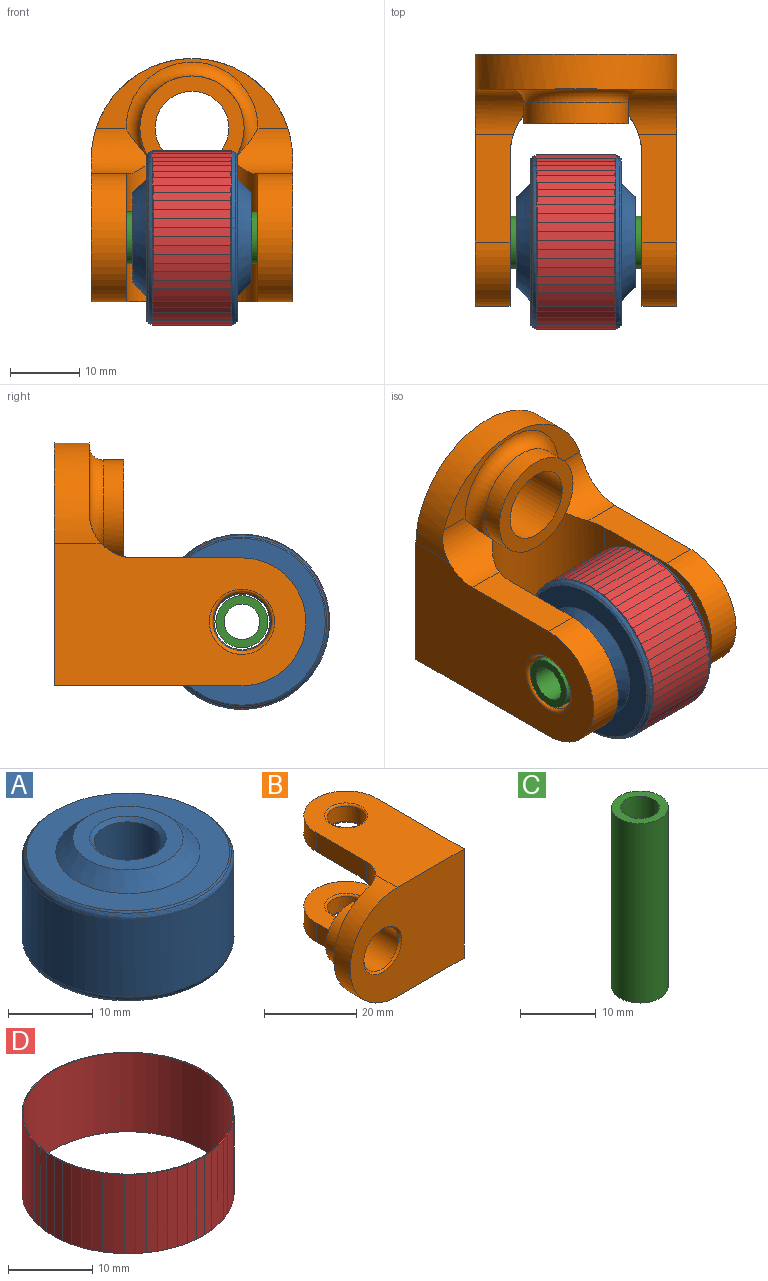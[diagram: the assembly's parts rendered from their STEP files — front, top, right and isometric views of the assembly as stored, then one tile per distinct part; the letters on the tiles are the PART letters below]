
ASSEMBLY  parts=4 mates=3
PART A: 14 faces, bbox 27.1x27.1x17 mm
  f0: cylinder r=4mm len=16mm, axis (0,0,-1), area 402.1mm2, adj f10,f11
  f1: cylinder r=12.5mm len=25mm, axis (0,0,-1), area 877.4mm2, adj f6,f7
  f2: plane 24x24mm, normal (0,0,1), area 225.4mm2, adj f5,f13
  f3: plane 24x24mm, normal (0,0,-1), area 225.4mm2, adj f4,f12
  f4: cone r=12.5mm half-angle=45deg, axis (0,0,1), area 22.3mm2, adj f3,f6
  f5: cone r=12mm half-angle=45deg, axis (0,0,-1), area 22.3mm2, adj f2,f7
  f6: torus R=11.5mm, axis (0,0,-1), area 61.2mm2, adj f1,f4
  f7: torus R=11.5mm, axis (0,0,1), area 61.2mm2, adj f1,f5
  f8: plane 13x13mm, normal (0,0,1), area 69.1mm2, adj f10,f13
  f9: plane 13x13mm, normal (0,0,-1), area 69.1mm2, adj f11,f12
  f10: cone r=4mm half-angle=45deg, axis (0,0,1), area 18.9mm2, adj f0,f8
  f11: cone r=4.5mm half-angle=45deg, axis (0,0,-1), area 18.9mm2, adj f0,f9
  f12: cone r=8.5mm half-angle=45deg, axis (0,0,1), area 133.3mm2, adj f3,f9
  f13: cone r=6.5mm half-angle=45deg, axis (0,0,-1), area 133.3mm2, adj f2,f8
PART B: 26 faces, bbox 36.8x36.2x29 mm
  f0: plane 29x27mm, normal (1,0,0), area 403.7mm2, adj f1,f4,f5,f9,f12,f13,f17,f21
  f1: cylinder r=9.2mm len=18.4mm, axis (0,0,-1), area 144.5mm2, adj f0,f3,f4,f5
  f2: cylinder r=4.2mm len=8.4mm, axis (0,0,-1), area 105.6mm2, adj f6,f7
  f3: plane 15.5x5.49mm, normal (-1,0,0), area 78mm2, adj f1,f4,f5,f21,f25
  f4: plane 36.2x20.5mm, normal (0,0,1), area 577.6mm2, adj f0,f1,f3,f7,f17,f22,f25
  f5: plane 21.7x18.4mm, normal (0,0,-1), area 293.6mm2, adj f0,f1,f3,f6,f21
  f6: torus R=4.7mm, axis (0,0,1), area 21.6mm2, adj f2,f5
  f7: torus R=4.7mm, axis (0,0,1), area 21.6mm2, adj f2,f4
  f8: plane 27.63x10.1mm, normal (0,1,0), area 61mm2, adj f20,f22,f24,f25
  f9: cylinder r=9.2mm len=18.4mm, axis (0,0,-1), area 144.5mm2, adj f0,f11,f12,f13
  f10: cylinder r=4.2mm len=8.4mm, axis (0,0,-1), area 105.6mm2, adj f14,f15
  f11: plane 15.5x5.49mm, normal (-1,0,0), area 78mm2, adj f9,f12,f13,f21,f24
  f12: plane 21.7x18.4mm, normal (0,0,1), area 293.6mm2, adj f0,f9,f11,f15,f21
  f13: plane 36.2x20.5mm, normal (0,0,-1), area 577.6mm2, adj f0,f9,f11,f14,f17,f22,f24
  f14: torus R=4.7mm, axis (0,0,1), area 21.6mm2, adj f10,f13
  f15: torus R=4.7mm, axis (0,0,1), area 21.6mm2, adj f10,f12
  f16: cylinder r=5.3mm len=10.6mm, axis (0,1,0), area 316.4mm2, adj f19,f23
  f17: plane 35x29mm, normal (0,-1,0), area 819.1mm2, adj f0,f4,f13,f22,f23
  f18: cylinder r=7.5mm len=15mm, axis (0,-1,0), area 141.4mm2, adj f19,f20
  f19: plane 15x15mm, normal (0,1,0), area 88.5mm2, adj f16,f18
  f20: torus R=9.5mm, axis (0,-1,0), area 119.9mm2, adj f8,f18,f21,f24,f25
  f21: cylinder r=9.5mm len=20.24mm, axis (-1,0,0), area 546.1mm2, adj f0,f3,f5,f11,f12,f20,f24,f25
  f22: cylinder r=14.5mm len=29mm, axis (0,1,0), area 232.5mm2, adj f4,f8,f13,f17,f24,f25
  f23: cone r=5.3mm half-angle=45deg, axis (0,-1,0), area 24.7mm2, adj f16,f17
  f24: cylinder r=6.5mm len=8.71mm, axis (0,0,-1), area 68.7mm2, adj f8,f11,f13,f20,f21,f22
  f25: cylinder r=6.5mm len=8.71mm, axis (0,0,-1), area 68.7mm2, adj f3,f4,f8,f20,f21,f22
PART C: 4 faces, bbox 7.5x7.5x29 mm
  f0: cylinder r=2.55mm len=29mm, axis (0,0,-1), area 464.6mm2, adj f2,f3
  f1: cylinder r=3.75mm len=29mm, axis (0,0,-1), area 683.3mm2, adj f2,f3
  f2: plane 7.5x7.5mm, normal (0,0,1), area 23.8mm2, adj f0,f1
  f3: plane 7.5x7.5mm, normal (0,0,-1), area 23.8mm2, adj f0,f1
PART D: 63 faces, bbox 25.2x25.2x11.5 mm
  f0: plane 11.5x1.04mm, normal (0.62,0.79,0), area 15.2mm2, adj f1,f60,f61,f62
  f1: plane 11.5x1.12mm, normal (0.53,0.85,0), area 15.2mm2, adj f0,f2,f61,f62
  f2: plane 11.5x1.19mm, normal (0.44,0.9,0), area 15.2mm2, adj f1,f3,f61,f62
  f3: plane 11.5x1.24mm, normal (0.34,0.94,0), area 15.2mm2, adj f2,f4,f61,f62
  f4: plane 11.5x1.28mm, normal (0.24,0.97,0), area 15.2mm2, adj f3,f5,f61,f62
  f5: plane 11.5x1.31mm, normal (0.14,0.99,0), area 15.2mm2, adj f4,f6,f61,f62
  f6: plane 11.5x1.32mm, normal (0.03,1,0), area 15.2mm2, adj f5,f7,f61,f62
  f7: plane 11.5x1.32mm, normal (-0.07,1,0), area 15.2mm2, adj f6,f8,f61,f62
  f8: plane 11.5x1.3mm, normal (-0.17,0.98,0), area 15.2mm2, adj f7,f9,f61,f62
  f9: plane 11.5x1.27mm, normal (-0.28,0.96,0), area 15.2mm2, adj f8,f10,f61,f62
  f10: plane 11.5x1.22mm, normal (-0.38,0.93,0), area 15.2mm2, adj f9,f11,f61,f62
  f11: plane 11.5x1.17mm, normal (-0.47,0.88,0), area 15.2mm2, adj f10,f12,f61,f62
  f12: plane 11.5x1.09mm, normal (-0.56,0.83,0), area 15.2mm2, adj f11,f13,f61,f62
  f13: plane 11.5x1.01mm, normal (-0.64,0.77,0), area 15.2mm2, adj f12,f14,f61,f62
  f14: plane 11.5x0.95mm, normal (-0.72,0.69,0), area 15.2mm2, adj f13,f15,f61,f62
  f15: plane 11.5x1.04mm, normal (-0.79,0.62,0), area 15.2mm2, adj f14,f16,f61,f62
  f16: plane 11.5x1.12mm, normal (-0.85,0.53,0), area 15.2mm2, adj f15,f17,f61,f62
  f17: plane 11.5x1.19mm, normal (-0.9,0.44,0), area 15.2mm2, adj f16,f18,f61,f62
  f18: plane 11.5x1.24mm, normal (-0.94,0.34,0), area 15.2mm2, adj f17,f19,f61,f62
  f19: plane 11.5x1.28mm, normal (-0.97,0.24,0), area 15.2mm2, adj f18,f20,f61,f62
  f20: plane 11.5x1.31mm, normal (-0.99,0.14,0), area 15.2mm2, adj f19,f21,f61,f62
  f21: plane 11.5x1.32mm, normal (-1,0.03,0), area 15.2mm2, adj f20,f22,f61,f62
  f22: plane 11.5x1.32mm, normal (-1,-0.07,0), area 15.2mm2, adj f21,f23,f61,f62
  f23: plane 11.5x1.3mm, normal (-0.98,-0.17,0), area 15.2mm2, adj f22,f24,f61,f62
  f24: plane 11.5x1.27mm, normal (-0.96,-0.28,0), area 15.2mm2, adj f23,f25,f61,f62
  f25: plane 11.5x1.22mm, normal (-0.93,-0.38,0), area 15.2mm2, adj f24,f26,f61,f62
  f26: plane 11.5x1.17mm, normal (-0.88,-0.47,0), area 15.2mm2, adj f25,f27,f61,f62
  f27: plane 11.5x1.09mm, normal (-0.83,-0.56,0), area 15.2mm2, adj f26,f28,f61,f62
  f28: plane 11.5x1.01mm, normal (-0.77,-0.64,0), area 15.2mm2, adj f27,f29,f61,f62
  f29: plane 11.5x0.95mm, normal (-0.69,-0.72,0), area 15.2mm2, adj f28,f30,f61,f62
  f30: plane 11.5x1.04mm, normal (-0.62,-0.79,0), area 15.2mm2, adj f29,f31,f61,f62
  f31: plane 11.5x1.12mm, normal (-0.53,-0.85,0), area 15.2mm2, adj f30,f32,f61,f62
  f32: plane 11.5x1.19mm, normal (-0.44,-0.9,0), area 15.2mm2, adj f31,f33,f61,f62
  f33: plane 11.5x1.24mm, normal (-0.34,-0.94,0), area 15.2mm2, adj f32,f34,f61,f62
  f34: plane 11.5x1.28mm, normal (-0.24,-0.97,0), area 15.2mm2, adj f33,f35,f61,f62
  f35: plane 11.5x1.31mm, normal (-0.14,-0.99,0), area 15.2mm2, adj f34,f36,f61,f62
  f36: plane 11.5x1.32mm, normal (-0.03,-1,0), area 15.2mm2, adj f35,f37,f61,f62
  f37: plane 11.5x1.32mm, normal (0.07,-1,0), area 15.2mm2, adj f36,f38,f61,f62
  f38: plane 11.5x1.3mm, normal (0.17,-0.98,0), area 15.2mm2, adj f37,f39,f61,f62
  f39: plane 11.5x1.27mm, normal (0.28,-0.96,0), area 15.2mm2, adj f38,f40,f61,f62
  f40: plane 11.5x1.22mm, normal (0.38,-0.93,0), area 15.2mm2, adj f39,f41,f61,f62
  f41: plane 11.5x1.17mm, normal (0.47,-0.88,0), area 15.2mm2, adj f40,f42,f61,f62
  f42: plane 11.5x1.09mm, normal (0.56,-0.83,0), area 15.2mm2, adj f41,f43,f61,f62
  f43: plane 11.5x1.01mm, normal (0.64,-0.77,0), area 15.2mm2, adj f42,f44,f61,f62
  f44: plane 11.5x0.95mm, normal (0.72,-0.69,0), area 15.2mm2, adj f43,f45,f61,f62
  f45: plane 11.5x1.04mm, normal (0.79,-0.62,0), area 15.2mm2, adj f44,f46,f61,f62
  f46: plane 11.5x1.12mm, normal (0.85,-0.53,0), area 15.2mm2, adj f45,f47,f61,f62
  f47: plane 11.5x1.19mm, normal (0.9,-0.44,0), area 15.2mm2, adj f46,f48,f61,f62
  f48: plane 11.5x1.24mm, normal (0.94,-0.34,0), area 15.2mm2, adj f47,f49,f61,f62
  f49: plane 11.5x1.28mm, normal (0.97,-0.24,0), area 15.2mm2, adj f48,f50,f61,f62
  f50: plane 11.5x1.31mm, normal (0.99,-0.14,0), area 15.2mm2, adj f49,f51,f61,f62
  f51: plane 11.5x1.32mm, normal (1,-0.03,0), area 15.2mm2, adj f50,f52,f61,f62
  f52: plane 11.5x1.32mm, normal (1,0.07,0), area 15.2mm2, adj f51,f53,f61,f62
  f53: plane 11.5x1.3mm, normal (0.98,0.17,0), area 15.2mm2, adj f52,f54,f61,f62
  f54: plane 11.5x1.27mm, normal (0.96,0.28,0), area 15.2mm2, adj f53,f55,f61,f62
  f55: plane 11.5x1.22mm, normal (0.93,0.38,0), area 15.2mm2, adj f54,f56,f61,f62
  f56: plane 11.5x1.17mm, normal (0.88,0.47,0), area 15.2mm2, adj f55,f57,f61,f62
  f57: plane 11.5x1.09mm, normal (0.83,0.56,0), area 15.2mm2, adj f56,f58,f61,f62
  f58: plane 11.5x1.01mm, normal (0.77,0.64,0), area 15.2mm2, adj f57,f60,f61,f62
  f59: cylinder r=12.5mm len=25mm, axis (0,0,-1), area 903.2mm2, adj f61,f62
  f60: plane 11.5x0.95mm, normal (0.69,0.72,0), area 15.2mm2, adj f0,f58,f61,f62
  f61: plane 25.23x25.23mm, normal (0,0,1), area 8.3mm2, adj f0,f1,f2,f3,f4,f5,f6,f7
  f62: plane 25.23x25.23mm, normal (0,0,-1), area 8.3mm2, adj f0,f1,f2,f3,f4,f5,f6,f7
PLACE A rot(axis=(0,1,0),90deg) t=(-6.5,0,0)mm
PLACE B rot(axis=(0.71,0,-0.71),180deg) t=(-9.5,0,0)mm
PLACE C rot(axis=(0,-1,0),90deg) t=(14.5,0,0)mm
PLACE D rot(axis=(0,-1,0),90deg) t=(5.75,0,0)mm
MATE fastened A.f1 <-> D.f59  axis (-1,0,0) through (0,0,0)mm
MATE fastened A.f1 <-> C.f1  axis (-1,0,0) through (0,0,0)mm
MATE revolute B.f2 <-> C.f0  axis (-1,0,0) through (-14.5,0,0)mm
